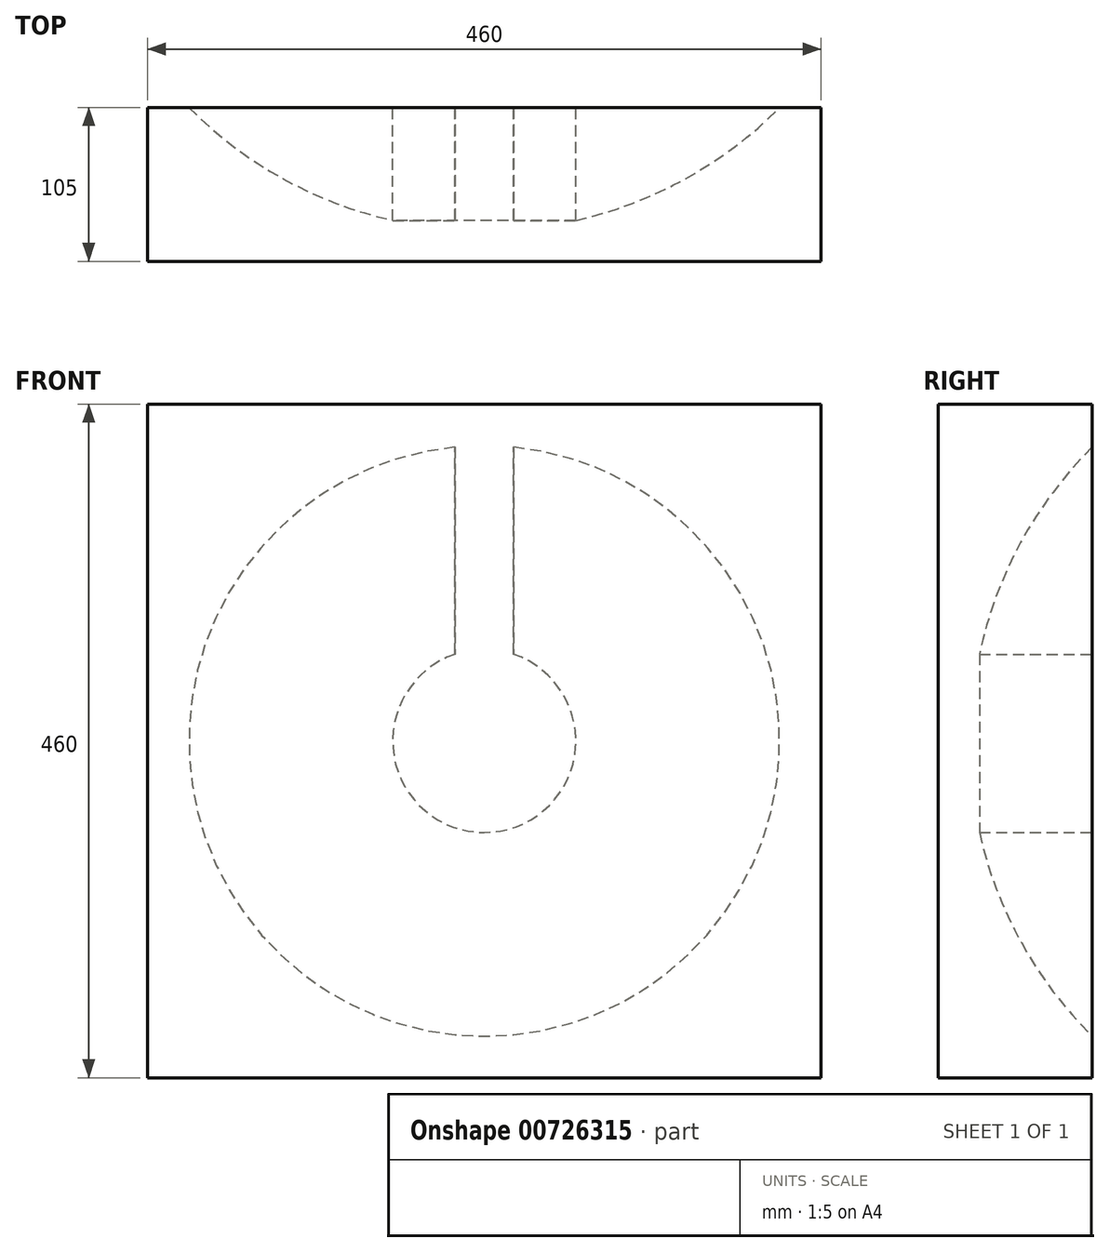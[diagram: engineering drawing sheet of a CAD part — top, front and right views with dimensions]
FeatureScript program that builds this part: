
annotation { "Feature Type Name" : "Feature", "Feature Type Description" : "" }
export const myFeature = defineFeature(function(context is Context, id is Id, definition is map)
    precondition{}
    {
        {
            var Q0;
            Q0=qCreatedBy(makeId("Front.planeOp"),FACE);
            var sketch = newSketch(context, id + "F0", { "sketchPlane" : qUnion([Q0])});
            skArc(sketch, "E0", {"start": v(284, 0) * mm, "mid": v(0, 284) * mm, "end": v(-284, 0) * mm});
            skPoint(sketch, "E1", {"position": v(-284, 0) * mm});
            skPoint(sketch, "E2", {"position": v(284, 0) * mm});
            skLineSegment(sketch, "E3", {"start": v(-284, 0) * mm, "end": v(284, 0) * mm});
            skSolve(sketch);
        }
        {
            var Q0;
            Q0=makeQuery(id+"F0.imprint","IMPRINT",FACE,{"disambiguationData":[TD([[makeQuery(id+"F0.imprint","IMPRINT",EDGE,{"derivedFrom":sQuery(id+"F0.wireOp",EDGE,"E0")}),1.0]])]});
            var Q1;
            Q1=sQuery(id+"F0.wireOp",EDGE,"E3");
            revolve(context, id + "F1", {"surfaceOperationType" : NewSurfaceOperationType.NEW, "entities" : qUnion([Q0]), "axis" : qUnion([Q1]), "revolveType" : RevolveType.FULL});
        }
        {
            var Q0;
            Q0=qCreatedBy(makeId("Front.planeOp"),FACE);
            cPlane(context, id + "F2", {"entities" : qUnion([Q0]), "cplaneType" : CPlaneType.OFFSET, "offset" : 200 * mm, "width" : 150 * mm, "height" : 150 * mm});
        }
        {
            var Q0;
            Q0=qCreatedBy(id+"F2.planeOp",FACE);
            var sketch = newSketch(context, id + "F3", { "sketchPlane" : qUnion([Q0])});
            skCircle(sketch, "E4", {"center": v(0, 0) * mm, "radius": 300 * mm});
            skSolve(sketch);
        }
        {
            var Q0;
            Q0=makeQuery(id+"F3.imprint","IMPRINT",FACE,{"disambiguationData":[TD([[makeQuery(id+"F3.imprint","IMPRINT",EDGE,{"derivedFrom":sQuery(id+"F3.wireOp",EDGE,"E4")}),1.0]])]});
            extrude(context, id + "F4", {"entities" : qUnion([Q0]), "operationType" : NewBodyOperationType.REMOVE, "oppositeDirection" : true, "depth" : 500 * mm, "offsetDistance" : 25 * mm});
        }
        {
            var Q0;
            Q0=qCreatedBy(makeId("Front.planeOp"),FACE);
            var sketch = newSketch(context, id + "F5", { "sketchPlane" : qUnion([Q0])});
            skCircle(sketch, "E5", {"center": v(0, 0) * mm, "radius": 62.5 * mm});
            skLineSegment(sketch, "E6.left", {"start": v(62.5, 0) * mm, "end": v(62.5, 0) * mm});
            skLineSegment(sketch, "E6.right", {"start": v(-62.5, 0) * mm, "end": v(-62.5, 0) * mm});
            skLineSegment(sketch, "E7.bottom", {"start": v(20, 224.59) * mm, "end": v(-20, 224.59) * mm});
            skLineSegment(sketch, "E7.top", {"start": v(20, 26) * mm, "end": v(-20, 26) * mm});
            skLineSegment(sketch, "E7.left", {"start": v(20, 224.59) * mm, "end": v(20, 26) * mm});
            skLineSegment(sketch, "E7.right", {"start": v(-20, 224.59) * mm, "end": v(-20, 26) * mm});
            skSolve(sketch);
        }
        {
            var Q0;
            {var subQ5=sQuery(id+"F5.wireOp",EDGE,"E7.bottom");Q0=makeQuery(id+"F5.imprint","IMPRINT",FACE,{"disambiguationData":[TD([[makeQuery(id+"F5.imprint","IMPRINT",EDGE,{"derivedFrom":subQ5}),1.0]])]});}
            var Q1;
            {var subQ5=sQuery(id+"F5.wireOp",EDGE,"E7.top");Q1=makeQuery(id+"F5.imprint","IMPRINT",FACE,{"disambiguationData":[TD([[makeQuery(id+"F5.imprint","IMPRINT",EDGE,{"derivedFrom":subQ5}),1.0]])]});}
            var Q2;
            {var subQ5=sQuery(id+"F5.wireOp",EDGE,"E7.top");Q2=makeQuery(id+"F5.imprint","IMPRINT",FACE,{"disambiguationData":[TD([[makeQuery(id+"F5.imprint","IMPRINT",EDGE,{"derivedFrom":subQ5}),-1.0]])]});}
            extrude(context, id + "F6", {"entities" : qUnion([Q0, Q1, Q2]), "operationType" : NewBodyOperationType.REMOVE, "depth" : 600 * mm, "offsetDistance" : 25 * mm});
        }
        {
            var Q0;
            Q0=qCreatedBy(id+"F2.planeOp",FACE);
            var sketch = newSketch(context, id + "F7", { "sketchPlane" : qUnion([Q0])});
            skLineSegment(sketch, "E8.bottom", {"start": v(230, -230) * mm, "end": v(-230, -230) * mm});
            skLineSegment(sketch, "E8.top", {"start": v(230, 230) * mm, "end": v(-230, 230) * mm});
            skLineSegment(sketch, "E8.left", {"start": v(230, -230) * mm, "end": v(230, 230) * mm});
            skLineSegment(sketch, "E8.right", {"start": v(-230, -230) * mm, "end": v(-230, 230) * mm});
            skPoint(sketch, "E8.middle", {"position": v(0, 0) * mm});
            skSolve(sketch);
        }
        {
            var Q0;
            Q0 = qSketchRegion(id + "F7", true);
            extrude(context, id + "F8", {"entities" : qUnion([Q0]), "depth" : 105 * mm, "offsetDistance" : 25 * mm});
        }
        {
            var Q0;
            Q0=makeQuery(id+"F1.opRevolve","SWEPT_BODY",BODY,{"disambiguationData":[OSD([sQuery(id+"F0.wireOp",EDGE,"E0"),sQuery(id+"F0.wireOp",EDGE,"E3")])]});
            var Q1;
            Q1=makeQuery(id+"F8.opExtrude","SWEPT_BODY",BODY,{"disambiguationData":[OSD([sQuery(id+"F7.wireOp",EDGE,"E8.bottom"),sQuery(id+"F7.wireOp",EDGE,"E8.top"),sQuery(id+"F7.wireOp",EDGE,"E8.left"),sQuery(id+"F7.wireOp",EDGE,"E8.right")])]});
            booleanBodies(context, id + "F9", {"operationType" : BooleanOperationType.SUBTRACTION, "tools" : qUnion([Q0]), "targets" : qUnion([Q1])});
        }
    });
